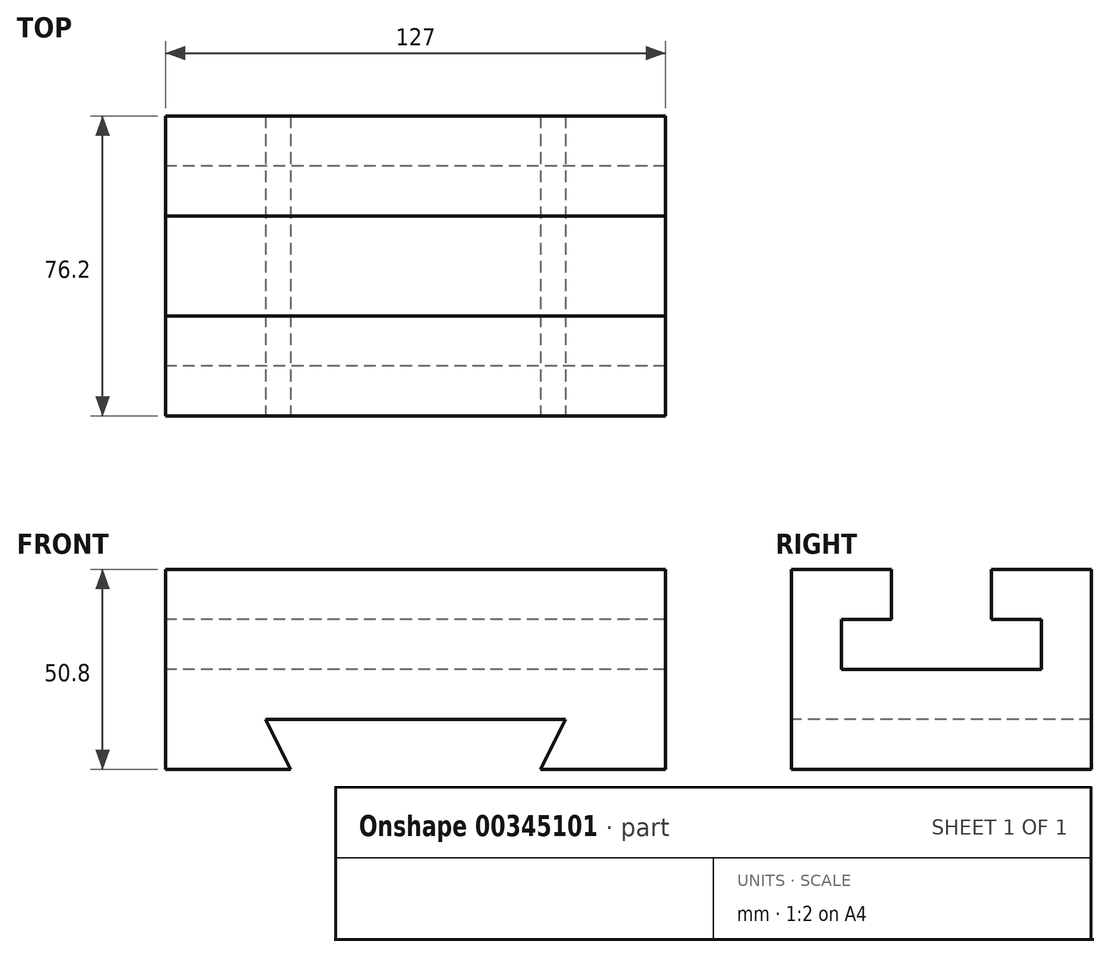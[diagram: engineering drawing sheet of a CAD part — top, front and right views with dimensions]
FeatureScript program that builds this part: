
annotation { "Feature Type Name" : "Feature", "Feature Type Description" : "" }
export const myFeature = defineFeature(function(context is Context, id is Id, definition is map)
    precondition{}
    {
        {
            var Q0;
            Q0=qCreatedBy(makeId("Right.planeOp"),FACE);
            var sketch = newSketch(context, id + "F0", { "sketchPlane" : qUnion([Q0])});
            skLineSegment(sketch, "E0", {"start": v(0, 0) * mm, "end": v(0, 50.8) * mm});
            skLineSegment(sketch, "E1", {"start": v(0, 50.8) * mm, "end": v(25.4, 50.8) * mm});
            skLineSegment(sketch, "E2", {"start": v(25.4, 50.8) * mm, "end": v(25.4, 38.1) * mm});
            skLineSegment(sketch, "E3", {"start": v(25.4, 38.1) * mm, "end": v(12.7, 38.1) * mm});
            skLineSegment(sketch, "E4", {"start": v(12.7, 38.1) * mm, "end": v(12.7, 25.4) * mm});
            skLineSegment(sketch, "E5", {"start": v(12.7, 25.4) * mm, "end": v(63.5, 25.4) * mm});
            skLineSegment(sketch, "E6", {"start": v(63.5, 25.4) * mm, "end": v(63.5, 38.1) * mm});
            skLineSegment(sketch, "E7", {"start": v(63.5, 38.1) * mm, "end": v(50.8, 38.1) * mm});
            skLineSegment(sketch, "E8", {"start": v(50.8, 38.1) * mm, "end": v(50.8, 50.8) * mm});
            skLineSegment(sketch, "E9", {"start": v(50.8, 50.8) * mm, "end": v(76.2, 50.8) * mm});
            skLineSegment(sketch, "E10", {"start": v(76.2, 50.8) * mm, "end": v(76.2, 0) * mm});
            skLineSegment(sketch, "E11", {"start": v(76.2, 0) * mm, "end": v(0, 0) * mm});
            skSolve(sketch);
        }
        {
            var Q0;
            Q0 = qSketchRegion(id + "F0", true);
            extrude(context, id + "F1", {"entities" : qUnion([Q0]), "depth" : 127 * mm});
        }
        {
            var Q0;
            Q0=makeQuery(id+"F1.opExtrude","SWEPT_FACE",FACE,{"disambiguationData":[OSD([sQuery(id+"F0.wireOp",EDGE,"E0")])]});
            var sketch = newSketch(context, id + "F2", { "sketchPlane" : qUnion([Q0])});
            skLineSegment(sketch, "E12", {"start": v(95.25, 0) * mm, "end": v(101.6, 12.7) * mm});
            skLineSegment(sketch, "E13", {"start": v(101.6, 12.7) * mm, "end": v(25.4, 12.7) * mm});
            skLineSegment(sketch, "E14", {"start": v(25.4, 12.7) * mm, "end": v(31.75, 0) * mm});
            skLineSegment(sketch, "E15", {"start": v(31.75, 0) * mm, "end": v(95.25, 0) * mm});
            skSolve(sketch);
        }
        {
            var Q0;
            Q0 = qSketchRegion(id + "F2", true);
            extrude(context, id + "F3", {"entities" : qUnion([Q0]), "operationType" : NewBodyOperationType.REMOVE, "oppositeDirection" : true, "depth" : 76.2 * mm});
        }
    });
